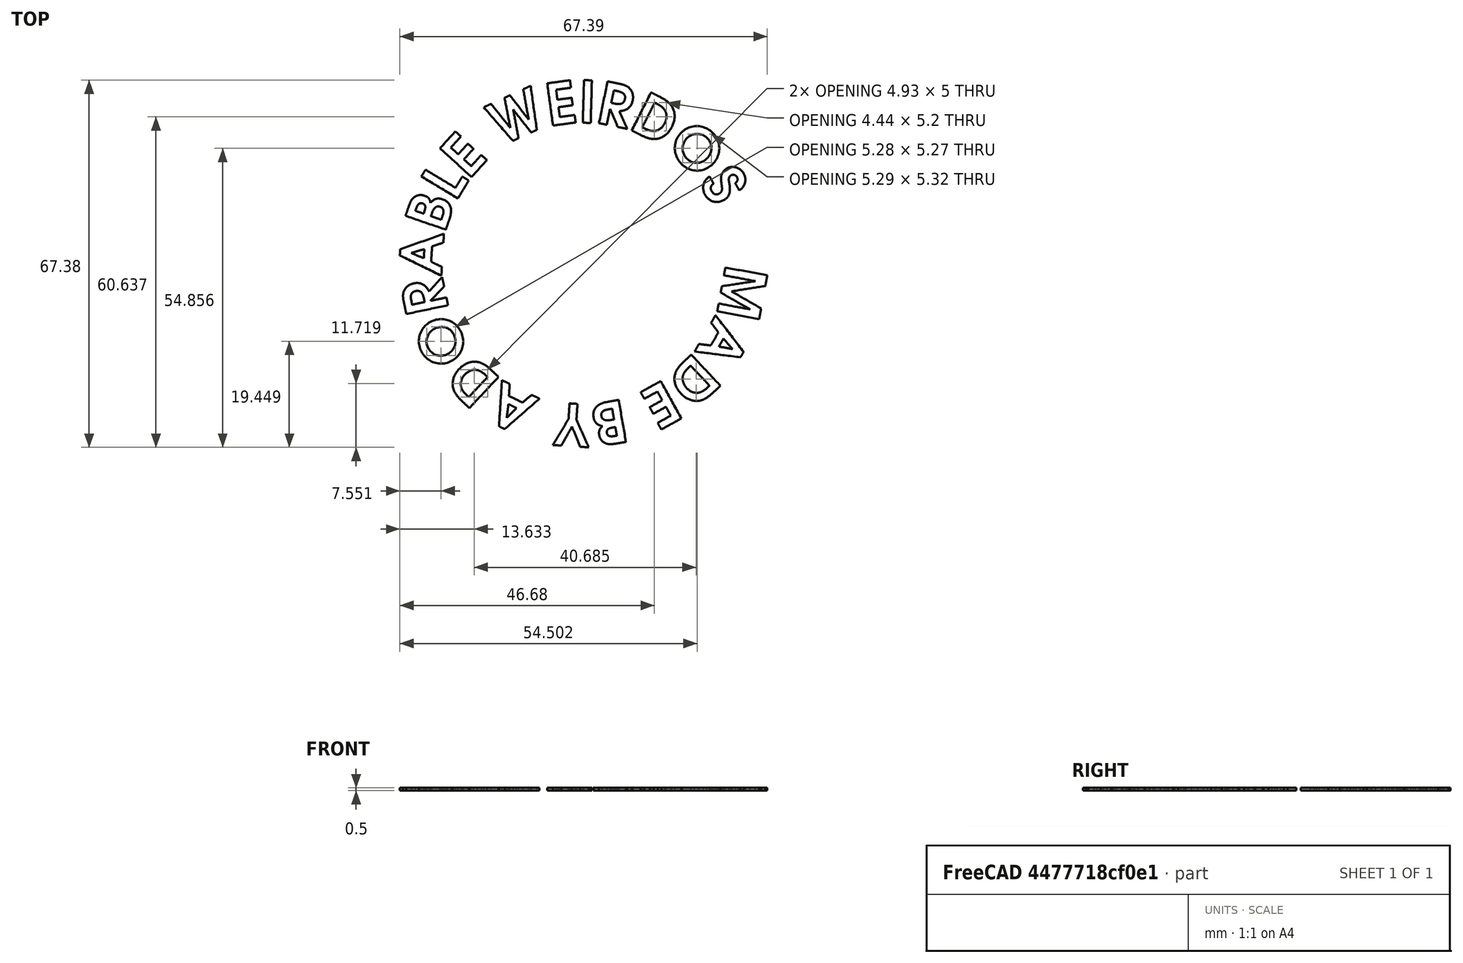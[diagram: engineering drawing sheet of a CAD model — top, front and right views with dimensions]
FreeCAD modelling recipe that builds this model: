
FCSTD DOCUMENT  (FreeCAD 0.18R4 (GitTag))
Label: MadeByAdorableWeirdos
License: All rights reserved
LicenseURL: http://en.wikipedia.org/wiki/All_rights_reserved
objects: Part::Feature×35, Part::Extrusion×35, Part::MultiFuse×2, Part::Mirroring×1, Part::Cut×1
note: 74 computed .brp shape members not serialized (recipe doc carries the construction recipe); baked Part::Feature solids carry a one-line shape summary decoded from their .brp

FEATURE [Part::Feature] Face
  shape: bbox 9.184 x 9.463 x 2e-07 mm, 1 faces, 0 solids (baked)
FEATURE [Part::Feature] Face001
  shape: bbox 2.651 x 2.627 x 2e-07 mm, 1 faces, 0 solids (baked)
FEATURE [Part::Feature] Face002
  shape: bbox 8.53 x 8.577 x 2e-07 mm, 1 faces, 0 solids (baked)
FEATURE [Part::Feature] Face003
  shape: bbox 2.409 x 2.217 x 2e-07 mm, 1 faces, 0 solids (baked)
FEATURE [Part::Feature] Face004
  shape: bbox 7.415 x 8.972 x 2e-07 mm, 1 faces, 0 solids (baked)
FEATURE [Part::Feature] Face005
  shape: bbox 8.497 x 8.592 x 2e-07 mm, 1 faces, 0 solids (baked)
FEATURE [Part::Feature] Face006
  shape: bbox 5.582 x 5.568 x 2e-07 mm, 1 faces, 0 solids (baked)
FEATURE [Part::Feature] Face007
  shape: bbox 8.613 x 8.371 x 2e-07 mm, 1 faces, 0 solids (baked)
FEATURE [Part::Feature] Face008
  shape: bbox 9.744 x 10.08 x 2e-07 mm, 1 faces, 0 solids (baked)
FEATURE [Part::Feature] Face009
  shape: bbox 8.554 x 8.603 x 2e-07 mm, 1 faces, 0 solids (baked)
FEATURE [Part::Feature] Face010
  shape: bbox 5.568 x 5.6 x 2e-07 mm, 1 faces, 0 solids (baked)
FEATURE [Part::Feature] Face011
  shape: bbox 1.664 x 7.858 x 2e-07 mm, 1 faces, 0 solids (baked)
FEATURE [Part::Feature] Face012
  shape: bbox 4.986 x 5.066 x 2e-07 mm, 1 faces, 0 solids (baked)
FEATURE [Part::Feature] Face013
  shape: bbox 1.885 x 1.992 x 2e-07 mm, 1 faces, 0 solids (baked)
FEATURE [Part::Feature] Face014
  shape: bbox 4.984 x 5.061 x 2e-07 mm, 1 faces, 0 solids (baked)
FEATURE [Part::Feature] Face015
  shape: bbox 4.509 x 5.218 x 2e-07 mm, 1 faces, 0 solids (baked)
FEATURE [Part::Feature] Face016
  shape: bbox 8.682 x 5.276 x 2e-07 mm, 1 faces, 0 solids (baked)
FEATURE [Part::Feature] Face017
  shape: bbox 8.075 x 7.669 x 2e-07 mm, 1 faces, 0 solids (baked)
FEATURE [Part::Feature] Face018
  shape: bbox 6.14 x 8.179 x 2e-07 mm, 1 faces, 0 solids (baked)
FEATURE [Part::Feature] Face019
  shape: bbox 6.579 x 8.066 x 2e-07 mm, 1 faces, 0 solids (baked)
FEATURE [Part::Feature] Face020
  shape: bbox 7.94 x 8.569 x 2e-07 mm, 1 faces, 0 solids (baked)
FEATURE [Part::Feature] Face021
  shape: bbox 8.573 x 8.602 x 2e-07 mm, 1 faces, 0 solids (baked)
FEATURE [Part::Feature] Face022
  shape: bbox 1.801 x 2.496 x 2e-07 mm, 1 faces, 0 solids (baked)
FEATURE [Part::Feature] Face023
  shape: bbox 5.216 x 8.315 x 2e-07 mm, 1 faces, 0 solids (baked)
FEATURE [Part::Feature] Face024
  shape: bbox 1.906 x 1.772 x 2e-07 mm, 1 faces, 0 solids (baked)
FEATURE [Part::Feature] Face025
  shape: bbox 2.417 x 1.669 x 2e-07 mm, 1 faces, 0 solids (baked)
FEATURE [Part::Feature] Face026
  shape: bbox 8.316 x 6.798 x 2e-07 mm, 1 faces, 0 solids (baked)
FEATURE [Part::Feature] Face027
  shape: bbox 2.379 x 2.512 x 2e-07 mm, 1 faces, 0 solids (baked)
FEATURE [Part::Feature] Face028
  shape: bbox 8.512 x 6.398 x 2e-07 mm, 1 faces, 0 solids (baked)
FEATURE [Part::Feature] Face029
  shape: bbox 6.283 x 8.728 x 2e-07 mm, 1 faces, 0 solids (baked)
FEATURE [Part::Feature] Face030
  shape: bbox 2.64 x 2.607 x 2e-07 mm, 1 faces, 0 solids (baked)
FEATURE [Part::Feature] Face031
  shape: bbox 7.999 x 6.686 x 2e-07 mm, 1 faces, 0 solids (baked)
FEATURE [Part::Feature] Face032
  shape: bbox 2.472 x 1.907 x 2e-07 mm, 1 faces, 0 solids (baked)
FEATURE [Part::Feature] Face033
  shape: bbox 7.462 x 8.878 x 2e-07 mm, 1 faces, 0 solids (baked)
FEATURE [Part::Feature] Face034
  shape: bbox 8.985 x 7.716 x 2e-07 mm, 1 faces, 0 solids (baked)
FEATURE [Part::Extrusion] Extrude
  Base = -> Face
  Dir = (0,0,1)
  DirMode = 2
  FaceMakerClass = Part::FaceMakerBullseye
  LengthFwd = 0.5
  LengthRev = 0
  Solid = false
  Symmetric = false
FEATURE [Part::Extrusion] Extrude001  label="nExtrude001"
  Base = -> Face001
  Dir = (0,0,-1)
  DirMode = 2
  FaceMakerClass = Part::FaceMakerBullseye
  LengthFwd = 0.5
  LengthRev = 0
  Solid = false
  Symmetric = false
FEATURE [Part::Extrusion] Extrude002
  Base = -> Face002
  Dir = (0,0,1)
  DirMode = 2
  FaceMakerClass = Part::FaceMakerBullseye
  LengthFwd = 0.5
  LengthRev = 0
  Solid = false
  Symmetric = false
FEATURE [Part::Extrusion] Extrude003  label="nExtrude003"
  Base = -> Face003
  Dir = (0,0,-1)
  DirMode = 2
  FaceMakerClass = Part::FaceMakerBullseye
  LengthFwd = 0.5
  LengthRev = 0
  Solid = false
  Symmetric = false
FEATURE [Part::Extrusion] Extrude004
  Base = -> Face004
  Dir = (0,0,1)
  DirMode = 2
  FaceMakerClass = Part::FaceMakerBullseye
  LengthFwd = 0.5
  LengthRev = 0
  Solid = false
  Symmetric = false
FEATURE [Part::Extrusion] Extrude005
  Base = -> Face005
  Dir = (0,0,1)
  DirMode = 2
  FaceMakerClass = Part::FaceMakerBullseye
  LengthFwd = 0.5
  LengthRev = 0
  Solid = false
  Symmetric = false
FEATURE [Part::Extrusion] Extrude006  label="nExtrude006"
  Base = -> Face006
  Dir = (0,0,-1)
  DirMode = 2
  FaceMakerClass = Part::FaceMakerBullseye
  LengthFwd = 0.5
  LengthRev = 0
  Solid = false
  Symmetric = false
FEATURE [Part::Extrusion] Extrude007
  Base = -> Face007
  Dir = (0,0,1)
  DirMode = 2
  FaceMakerClass = Part::FaceMakerBullseye
  LengthFwd = 0.5
  LengthRev = 0
  Solid = false
  Symmetric = false
FEATURE [Part::Extrusion] Extrude008
  Base = -> Face008
  Dir = (0,0,1)
  DirMode = 2
  FaceMakerClass = Part::FaceMakerBullseye
  LengthFwd = 0.5
  LengthRev = 0
  Solid = false
  Symmetric = false
FEATURE [Part::Extrusion] Extrude009
  Base = -> Face009
  Dir = (0,0,1)
  DirMode = 2
  FaceMakerClass = Part::FaceMakerBullseye
  LengthFwd = 0.5
  LengthRev = 0
  Solid = false
  Symmetric = false
FEATURE [Part::Extrusion] Extrude010  label="nExtrude010"
  Base = -> Face010
  Dir = (0,0,-1)
  DirMode = 2
  FaceMakerClass = Part::FaceMakerBullseye
  LengthFwd = 0.5
  LengthRev = 0
  Solid = false
  Symmetric = false
FEATURE [Part::Extrusion] Extrude011
  Base = -> Face011
  Dir = (0,0,1)
  DirMode = 2
  FaceMakerClass = Part::FaceMakerBullseye
  LengthFwd = 0.5
  LengthRev = 0
  Solid = false
  Symmetric = false
FEATURE [Part::Extrusion] Extrude012  label="nExtrude012"
  Base = -> Face012
  Dir = (0,0,-1)
  DirMode = 2
  FaceMakerClass = Part::FaceMakerBullseye
  LengthFwd = 0.5
  LengthRev = 0
  Solid = false
  Symmetric = false
FEATURE [Part::Extrusion] Extrude013  label="nExtrude013"
  Base = -> Face013
  Dir = (0,0,-1)
  DirMode = 2
  FaceMakerClass = Part::FaceMakerBullseye
  LengthFwd = 0.5
  LengthRev = 0
  Solid = false
  Symmetric = false
FEATURE [Part::Extrusion] Extrude014  label="nExtrude014"
  Base = -> Face014
  Dir = (0,0,-1)
  DirMode = 2
  FaceMakerClass = Part::FaceMakerBullseye
  LengthFwd = 0.5
  LengthRev = 0
  Solid = false
  Symmetric = false
FEATURE [Part::Extrusion] Extrude015  label="nExtrude015"
  Base = -> Face015
  Dir = (0,0,-1)
  DirMode = 2
  FaceMakerClass = Part::FaceMakerBullseye
  LengthFwd = 0.5
  LengthRev = 0
  Solid = false
  Symmetric = false
FEATURE [Part::Extrusion] Extrude016
  Base = -> Face016
  Dir = (0,0,1)
  DirMode = 2
  FaceMakerClass = Part::FaceMakerBullseye
  LengthFwd = 0.5
  LengthRev = 0
  Solid = false
  Symmetric = false
FEATURE [Part::Extrusion] Extrude017
  Base = -> Face017
  Dir = (0,0,1)
  DirMode = 2
  FaceMakerClass = Part::FaceMakerBullseye
  LengthFwd = 0.5
  LengthRev = 0
  Solid = false
  Symmetric = false
FEATURE [Part::Extrusion] Extrude018
  Base = -> Face018
  Dir = (0,0,1)
  DirMode = 2
  FaceMakerClass = Part::FaceMakerBullseye
  LengthFwd = 0.5
  LengthRev = 0
  Solid = false
  Symmetric = false
FEATURE [Part::Extrusion] Extrude019
  Base = -> Face019
  Dir = (0,0,1)
  DirMode = 2
  FaceMakerClass = Part::FaceMakerBullseye
  LengthFwd = 0.5
  LengthRev = 0
  Solid = false
  Symmetric = false
FEATURE [Part::Extrusion] Extrude020
  Base = -> Face020
  Dir = (0,0,1)
  DirMode = 2
  FaceMakerClass = Part::FaceMakerBullseye
  LengthFwd = 0.5
  LengthRev = 0
  Solid = false
  Symmetric = false
FEATURE [Part::Extrusion] Extrude021
  Base = -> Face021
  Dir = (0,0,1)
  DirMode = 2
  FaceMakerClass = Part::FaceMakerBullseye
  LengthFwd = 0.5
  LengthRev = 0
  Solid = false
  Symmetric = false
FEATURE [Part::Extrusion] Extrude022  label="nExtrude022"
  Base = -> Face022
  Dir = (0,0,-1)
  DirMode = 2
  FaceMakerClass = Part::FaceMakerBullseye
  LengthFwd = 0.5
  LengthRev = 0
  Solid = false
  Symmetric = false
FEATURE [Part::Extrusion] Extrude023
  Base = -> Face023
  Dir = (0,0,1)
  DirMode = 2
  FaceMakerClass = Part::FaceMakerBullseye
  LengthFwd = 0.5
  LengthRev = 0
  Solid = false
  Symmetric = false
FEATURE [Part::Extrusion] Extrude024  label="nExtrude024"
  Base = -> Face024
  Dir = (0,0,-1)
  DirMode = 2
  FaceMakerClass = Part::FaceMakerBullseye
  LengthFwd = 0.5
  LengthRev = 0
  Solid = false
  Symmetric = false
FEATURE [Part::Extrusion] Extrude025  label="nExtrude025"
  Base = -> Face025
  Dir = (0,0,-1)
  DirMode = 2
  FaceMakerClass = Part::FaceMakerBullseye
  LengthFwd = 0.5
  LengthRev = 0
  Solid = false
  Symmetric = false
FEATURE [Part::Extrusion] Extrude026
  Base = -> Face026
  Dir = (0,0,1)
  DirMode = 2
  FaceMakerClass = Part::FaceMakerBullseye
  LengthFwd = 0.5
  LengthRev = 0
  Solid = false
  Symmetric = false
FEATURE [Part::Extrusion] Extrude027  label="nExtrude027"
  Base = -> Face027
  Dir = (0,0,-1)
  DirMode = 2
  FaceMakerClass = Part::FaceMakerBullseye
  LengthFwd = 0.5
  LengthRev = 0
  Solid = false
  Symmetric = false
FEATURE [Part::Extrusion] Extrude028
  Base = -> Face028
  Dir = (0,0,1)
  DirMode = 2
  FaceMakerClass = Part::FaceMakerBullseye
  LengthFwd = 0.5
  LengthRev = 0
  Solid = false
  Symmetric = false
FEATURE [Part::Extrusion] Extrude029
  Base = -> Face029
  Dir = (0,0,1)
  DirMode = 2
  FaceMakerClass = Part::FaceMakerBullseye
  LengthFwd = 0.5
  LengthRev = 0
  Solid = false
  Symmetric = false
FEATURE [Part::Extrusion] Extrude030  label="nExtrude030"
  Base = -> Face030
  Dir = (0,0,-1)
  DirMode = 2
  FaceMakerClass = Part::FaceMakerBullseye
  LengthFwd = 0.5
  LengthRev = 0
  Solid = false
  Symmetric = false
FEATURE [Part::Extrusion] Extrude031
  Base = -> Face031
  Dir = (0,0,1)
  DirMode = 2
  FaceMakerClass = Part::FaceMakerBullseye
  LengthFwd = 0.5
  LengthRev = 0
  Solid = false
  Symmetric = false
FEATURE [Part::Extrusion] Extrude032  label="nExtrude032"
  Base = -> Face032
  Dir = (0,0,-1)
  DirMode = 2
  FaceMakerClass = Part::FaceMakerBullseye
  LengthFwd = 0.5
  LengthRev = 0
  Solid = false
  Symmetric = false
FEATURE [Part::Extrusion] Extrude033
  Base = -> Face033
  Dir = (0,0,1)
  DirMode = 2
  FaceMakerClass = Part::FaceMakerBullseye
  LengthFwd = 0.5
  LengthRev = 0
  Solid = false
  Symmetric = false
FEATURE [Part::Extrusion] Extrude034
  Base = -> Face034
  Dir = (0,0,1)
  DirMode = 2
  FaceMakerClass = Part::FaceMakerBullseye
  LengthFwd = 0.5
  LengthRev = 0
  Solid = false
  Symmetric = false
FEATURE [Part::MultiFuse] Fusion  label="nExtrude"
  Shapes = -> [Extrude032,Extrude030,Extrude027,Extrude025,Extrude024,Extrude022,Extrude015,Extrude014,Extrude013,Extrude012,Extrude010,Extrude006,Extrude001,Extrude003]
FEATURE [Part::Mirroring] Part__Mirroring  label="nMadeByAdorableWeirdos"
  Base = (0,0,0)
  Normal = (0,0,1)
  Source = -> Fusion
FEATURE [Part::MultiFuse] Fusion001  label="pMadeByAdorableWeirdos"
  Shapes = -> [Extrude,Extrude018,Extrude020,Extrude002,Extrude009,Extrude007,Extrude008,Extrude005,Extrude004,Extrude011,Extrude016,Extrude017,Extrude019,Extrude021,Extrude023,Extrude026,Extrude029,Extrude031,Extrude033,Extrude034,Extrude028]
FEATURE [Part::Cut] Cut  label="MadeByAdorableWeirdos"
  Base = -> Fusion001
  Tool = -> Part__Mirroring
